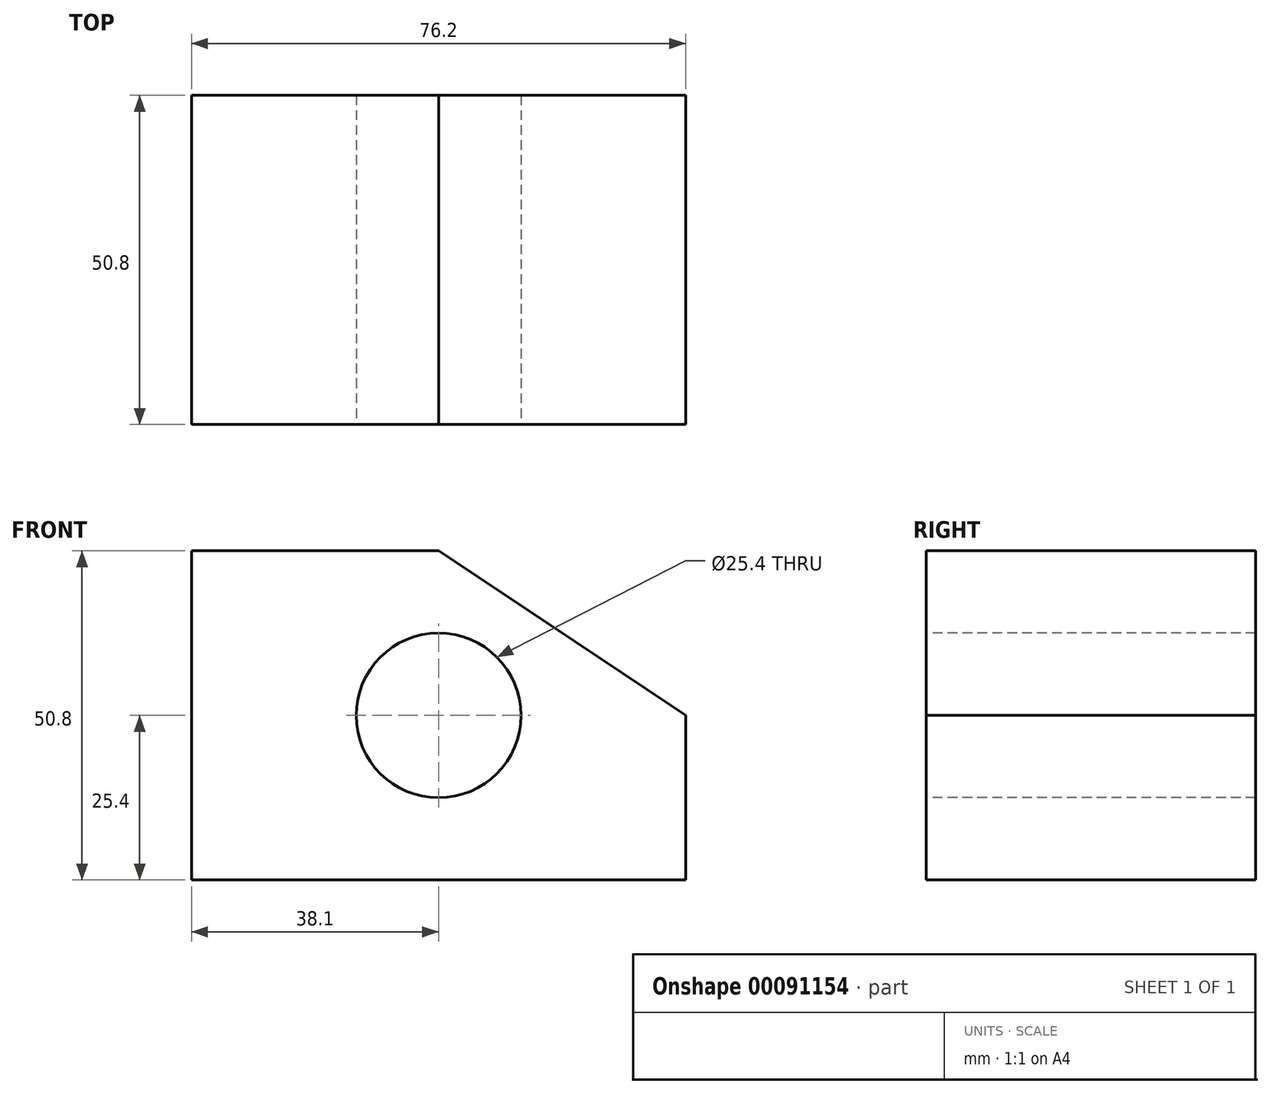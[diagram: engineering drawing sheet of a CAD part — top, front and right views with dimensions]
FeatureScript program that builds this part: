
annotation { "Feature Type Name" : "Feature", "Feature Type Description" : "" }
export const myFeature = defineFeature(function(context is Context, id is Id, definition is map)
    precondition{}
    {
        {
            var Q0;
            Q0=qCreatedBy(makeId("Front.planeOp"),FACE);
            var sketch = newSketch(context, id + "F0", { "sketchPlane" : qUnion([Q0])});
            skLineSegment(sketch, "E0", {"start": v(0, 0) * mm, "end": v(0, 50.8) * mm});
            skLineSegment(sketch, "E1", {"start": v(0, 50.8) * mm, "end": v(38.1, 50.8) * mm});
            skLineSegment(sketch, "E2", {"start": v(38.1, 50.8) * mm, "end": v(76.2, 25.4) * mm});
            skLineSegment(sketch, "E3", {"start": v(76.2, 25.4) * mm, "end": v(76.2, 0) * mm});
            skLineSegment(sketch, "E4", {"start": v(76.2, 0) * mm, "end": v(0, 0) * mm});
            skSolve(sketch);
        }
        {
            var Q0;
            Q0=makeQuery(id+"F0.imprint","IMPRINT",FACE,{"disambiguationData":[TD([[makeQuery(id+"F0.imprint","IMPRINT",EDGE,{"derivedFrom":sQuery(id+"F0.wireOp",EDGE,"E0")}),-1.0]])]});
            extrude(context, id + "F1", {"entities" : qUnion([Q0]), "depth" : 50.8 * mm});
        }
        {
            var Q0;
            Q0=makeQuery(id+"F1.opExtrude","CAP_FACE",FACE,{"disambiguationData":[OSD([sQuery(id+"F0.wireOp",EDGE,"E0"),sQuery(id+"F0.wireOp",EDGE,"E1"),sQuery(id+"F0.wireOp",EDGE,"E2"),sQuery(id+"F0.wireOp",EDGE,"E3"),sQuery(id+"F0.wireOp",EDGE,"E4")])],"isStart":false});
            var sketch = newSketch(context, id + "F2", { "sketchPlane" : qUnion([Q0])});
            skCircle(sketch, "E5", {"center": v(38.1, 25.4) * mm, "radius": 12.7 * mm});
            skSolve(sketch);
        }
        {
            var Q0;
            Q0=sQuery(id+"F2.wireOp",VERTEX,"E5.center");
            var Q1;
            Q1=makeQuery(id+"F1.opExtrude","SWEPT_BODY",BODY,{"disambiguationData":[OSD([sQuery(id+"F0.wireOp",EDGE,"E0"),sQuery(id+"F0.wireOp",EDGE,"E1"),sQuery(id+"F0.wireOp",EDGE,"E2"),sQuery(id+"F0.wireOp",EDGE,"E3"),sQuery(id+"F0.wireOp",EDGE,"E4")])]});
            hole(context, id + "F3", {"style" : HoleStyle.SIMPLE, "endStyle" : HoleEndStyle.THROUGH, "holeDiameter" : 25.4 * mm, "locations" : qUnion([Q0]), "scope" : qUnion([Q1]), "isTappedThrough" : true});
        }
    });
